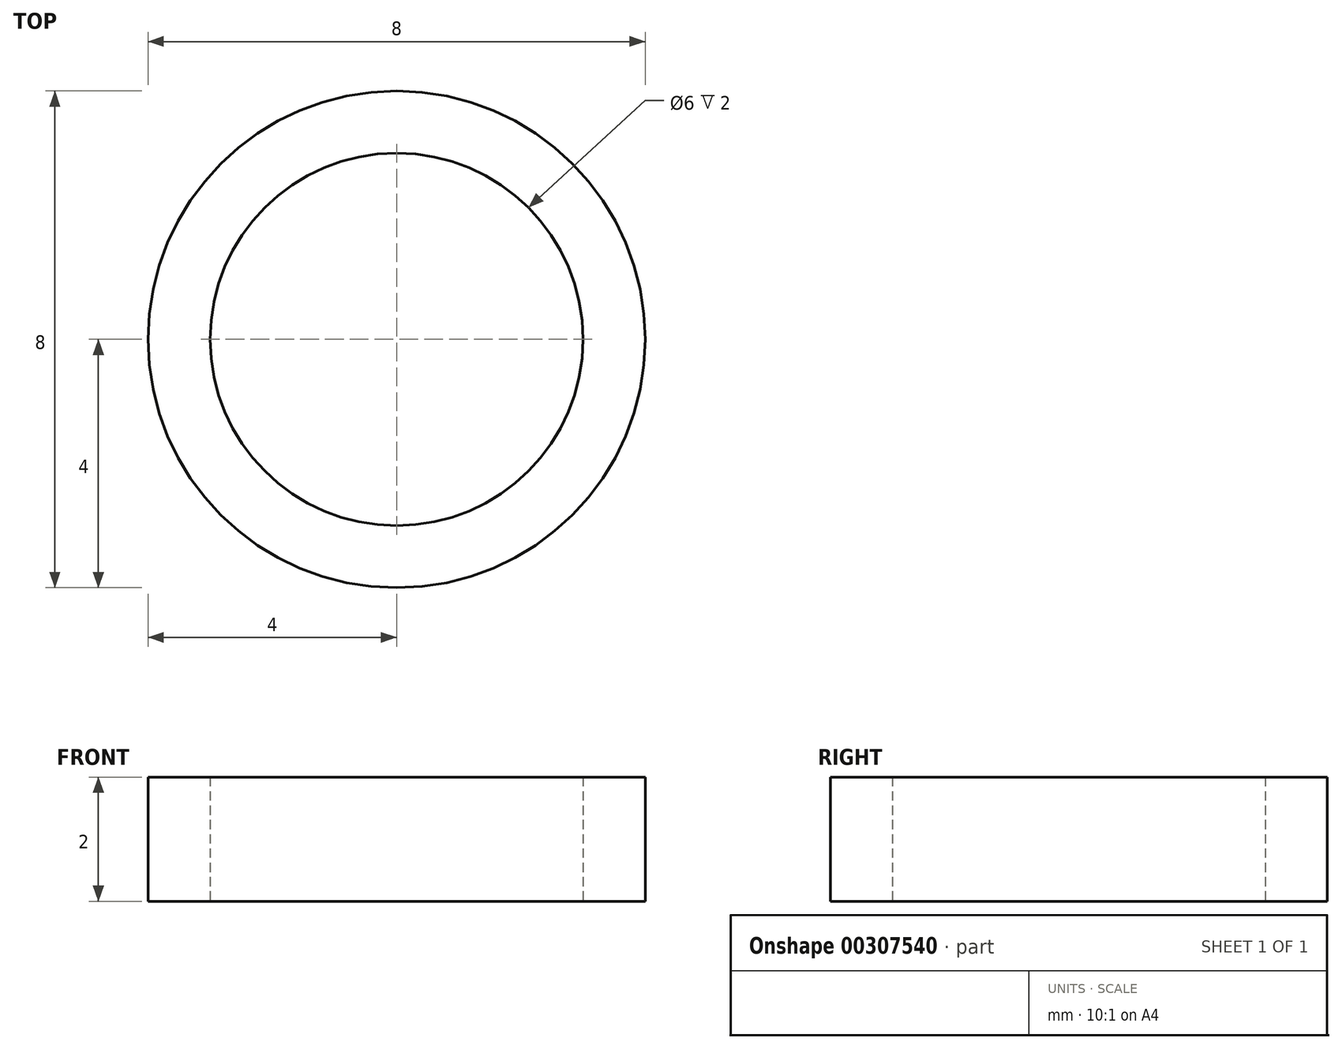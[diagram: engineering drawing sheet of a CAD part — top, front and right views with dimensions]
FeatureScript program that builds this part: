
annotation { "Feature Type Name" : "Feature", "Feature Type Description" : "" }
export const myFeature = defineFeature(function(context is Context, id is Id, definition is map)
    precondition{}
    {
        {
            var Q0;
            Q0=qCreatedBy(makeId("Top.planeOp"),FACE);
            var sketch = newSketch(context, id + "F0", { "sketchPlane" : qUnion([Q0])});
            skCircle(sketch, "E0", {"center": v(0, 0) * mm, "radius": 3 * mm});
            skCircle(sketch, "E1", {"center": v(0, 0) * mm, "radius": 4 * mm});
            skSolve(sketch);
        }
        {
            var Q0;
            Q0=makeQuery(id+"F0.imprint","IMPRINT",FACE,{"disambiguationData":[TD([[makeQuery(id+"F0.imprint","IMPRINT",EDGE,{"derivedFrom":sQuery(id+"F0.wireOp",EDGE,"E0")}),-1.0]])]});
            extrude(context, id + "F1", {"entities" : qUnion([Q0]), "depth" : 2 * mm, "offsetDistance" : 25 * mm});
        }
    });
